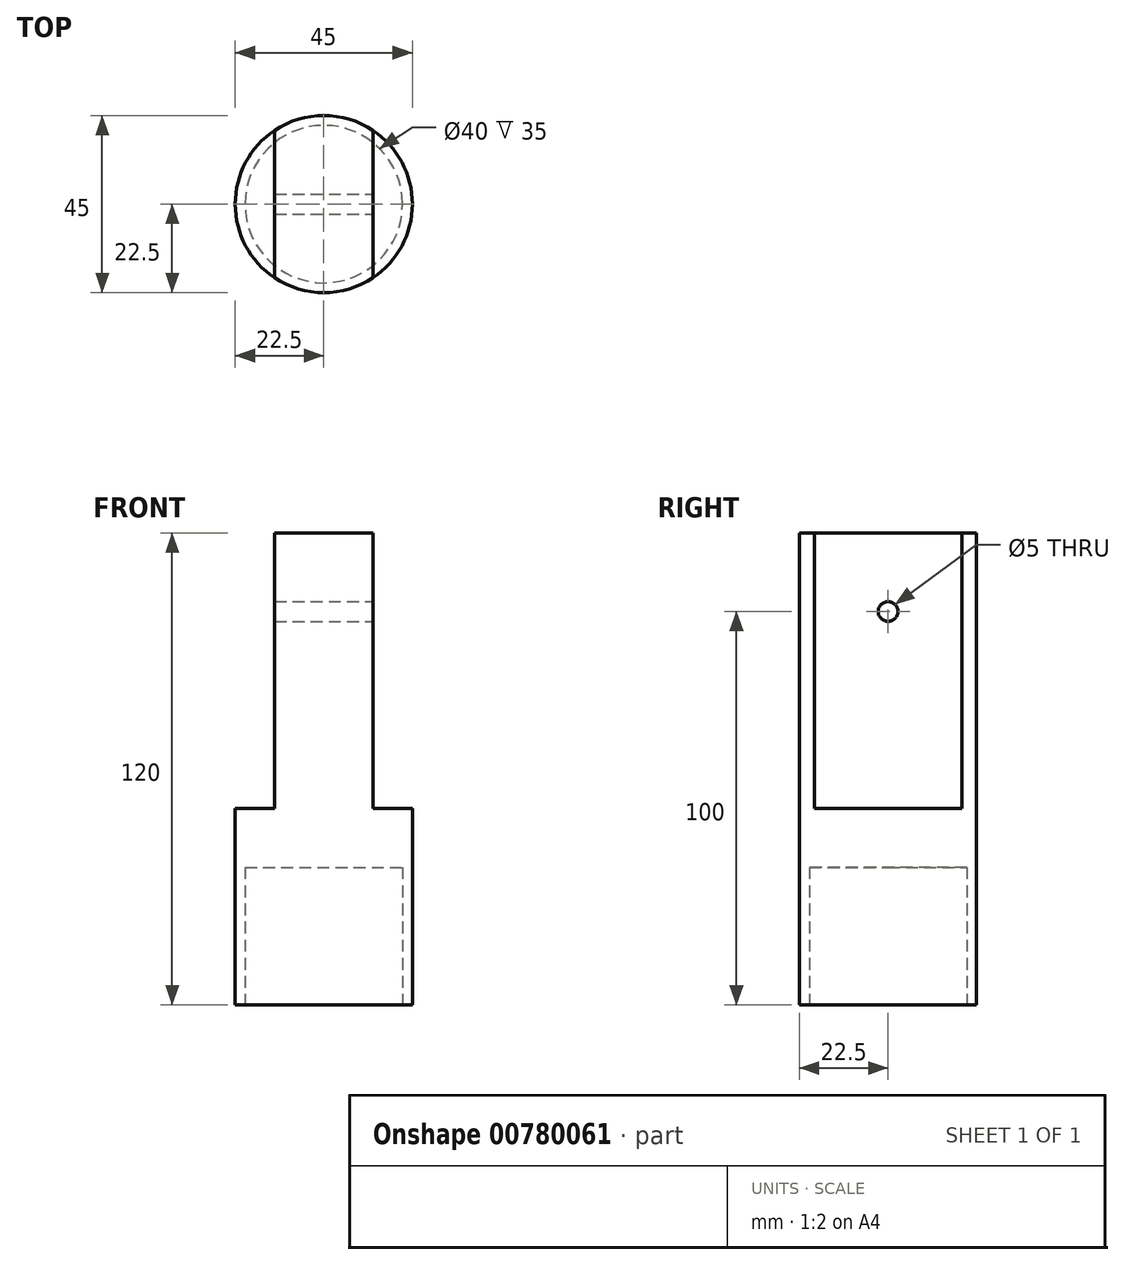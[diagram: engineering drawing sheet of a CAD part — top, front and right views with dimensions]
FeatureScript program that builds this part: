
annotation { "Feature Type Name" : "Feature", "Feature Type Description" : "" }
export const myFeature = defineFeature(function(context is Context, id is Id, definition is map)
    precondition{}
    {
        {
            var Q0;
            Q0=qCreatedBy(makeId("Top.planeOp"),FACE);
            var sketch = newSketch(context, id + "F0", { "sketchPlane" : qUnion([Q0])});
            skCircle(sketch, "E0", {"center": v(0, 0) * mm, "radius": 22.5 * mm});
            skSolve(sketch);
        }
        {
            var Q0;
            Q0=makeQuery(id+"F0.imprint","IMPRINT",FACE,{"disambiguationData":[TD([[makeQuery(id+"F0.imprint","IMPRINT",EDGE,{"derivedFrom":sQuery(id+"F0.wireOp",EDGE,"E0")}),1.0]])]});
            extrude(context, id + "F1", {"entities" : qUnion([Q0]), "depth" : 120 * mm, "offsetDistance" : 25 * mm});
        }
        {
            var Q0;
            Q0=makeQuery(id+"F1.opExtrude","CAP_FACE",FACE,{"disambiguationData":[OSD([sQuery(id+"F0.wireOp",EDGE,"E0")])],"isStart":false});
            var sketch = newSketch(context, id + "F2", { "sketchPlane" : qUnion([Q0])});
            skLineSegment(sketch, "E1", {"start": v(-12.5, 18.7) * mm, "end": v(-12.5, -18.7) * mm});
            skLineSegment(sketch, "E2", {"start": v(12.5, 18.7) * mm, "end": v(12.5, -18.7) * mm});
            skSolve(sketch);
        }
        {
            var Q0;
            {var subQ0=sQuery(id+"F2.wireOp",EDGE,"E1");Q0=makeQuery(id+"F2.imprint","IMPRINT",FACE,{"disambiguationData":[TD([[makeQuery(id+"F2.imprint","IMPRINT",EDGE,{"derivedFrom":subQ0}),-1.0]])]});}
            var Q1;
            {var subQ0=sQuery(id+"F2.wireOp",EDGE,"E2");Q1=makeQuery(id+"F2.imprint","IMPRINT",FACE,{"disambiguationData":[TD([[makeQuery(id+"F2.imprint","IMPRINT",EDGE,{"derivedFrom":subQ0}),1.0]])]});}
            var Q2;
            Q2=sQuery(id+"F2.wireOp",EDGE,"E1");
            var Q3;
            Q3=sQuery(id+"F2.wireOp",EDGE,"E2");
            extrude(context, id + "F3", {"entities" : qUnion([Q0, Q1]), "operationType" : NewBodyOperationType.REMOVE, "surfaceEntities" : qUnion([Q2, Q3]), "oppositeDirection" : true, "depth" : 70 * mm, "offsetDistance" : 25 * mm});
        }
        {
            var Q0;
            Q0=makeQuery(id+"F1.opExtrude","CAP_FACE",FACE,{"disambiguationData":[OSD([sQuery(id+"F0.wireOp",EDGE,"E0")])],"isStart":true});
            var sketch = newSketch(context, id + "F4", { "sketchPlane" : qUnion([Q0])});
            skCircle(sketch, "E3", {"center": v(0, 0) * mm, "radius": 20 * mm});
            skSolve(sketch);
        }
        {
            var Q0;
            Q0=makeQuery(id+"F4.imprint","IMPRINT",FACE,{"disambiguationData":[TD([[makeQuery(id+"F4.imprint","IMPRINT",EDGE,{"derivedFrom":sQuery(id+"F4.wireOp",EDGE,"E3")}),1.0]])]});
            extrude(context, id + "F5", {"entities" : qUnion([Q0]), "operationType" : NewBodyOperationType.REMOVE, "oppositeDirection" : true, "depth" : 35 * mm, "offsetDistance" : 25 * mm});
        }
        {
            var Q0;
            Q0=qCreatedBy(makeId("Right.planeOp"),FACE);
            var sketch = newSketch(context, id + "F6", { "sketchPlane" : qUnion([Q0])});
            skPoint(sketch, "E4", {"position": v(0, 100) * mm});
            skSolve(sketch);
        }
        {
            var Q0;
            Q0=sQuery(id+"F6.wireOp",VERTEX,"E4");
            var Q1;
            Q1=makeQuery(id+"F1.opExtrude","SWEPT_BODY",BODY,{"disambiguationData":[OSD([sQuery(id+"F0.wireOp",EDGE,"E0")])]});
            hole(context, id + "F7", {"style" : HoleStyle.SIMPLE, "endStyle" : HoleEndStyle.THROUGH, "holeDiameter" : 5 * mm, "majorDiameter" : 5 * mm, "isTappedThrough" : true, "tappedDepth" : 12 * mm, "tapClearance" : 3, "locations" : qUnion([Q0]), "scope" : qUnion([Q1])});
        }
        {
            var Q0;
            Q0=qCreatedBy(makeId("Right.planeOp"),FACE);
            var sketch = newSketch(context, id + "F8", { "sketchPlane" : qUnion([Q0])});
            skPoint(sketch, "E5", {"position": v(0, 100) * mm});
            skSolve(sketch);
        }
        {
            var Q0;
            Q0=sQuery(id+"F8.wireOp",VERTEX,"E5");
            var Q1;
            Q1=makeQuery(id+"F1.opExtrude","SWEPT_BODY",BODY,{"disambiguationData":[OSD([sQuery(id+"F0.wireOp",EDGE,"E0")])]});
            hole(context, id + "F9", {"style" : HoleStyle.SIMPLE, "endStyle" : HoleEndStyle.THROUGH, "oppositeDirection" : true, "holeDiameter" : 5 * mm, "majorDiameter" : 5 * mm, "isTappedThrough" : true, "tappedDepth" : 12 * mm, "tapClearance" : 3, "locations" : qUnion([Q0]), "scope" : qUnion([Q1])});
        }
    });
